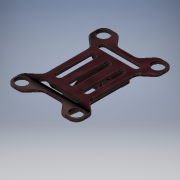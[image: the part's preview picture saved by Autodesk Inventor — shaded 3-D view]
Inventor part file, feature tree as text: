
AUTODESK INVENTOR PART (.ipt)
format: ipt  version: 2018 (Build 220112000, 112)  size: 1,005,056 bytes
history: native  units: in
note: dims shown in document units (in); Inventor stores cm internally (conversion verified against a paired STEP export)
features: fillet x13, extrude x9, sketch x9, delete_face x4, projected_geometry x2
ambient origin geometry x8: Origin, YZ Plane, XZ Plane, XY Plane, X Axis, Y Axis, Z Axis, Center Point
bodies: Solid1 (feature_tree)
feature tree (37):
  extrude  "Extrusion1"  Depth=0.189in
  extrude  "Extrusion2"  Depth=0.189in
  extrude  "Extrusion3"  Depth=0.0591in
  extrude  "Extrusion4"  Depth=1.1181in
  extrude  "Extrusion5"  Depth=0.5906in TaperAngle=0.0deg
  extrude  "Extrusion6"  Depth=0.315in
  delete_face  "Delete Face1"
  delete_face  "Delete Face2"
  delete_face  "Delete Face3"
  extrude  "Extrusion11"  Depth=0.1575in
  delete_face  "Delete Face4"
  extrude  "Extrusion12"  Depth=0.3937in TaperAngle=0.0deg
  extrude  "Extrusion13"  Depth=0.1181in TaperAngle=0.0deg
  fillet  "Fillet9"  Radius=0.0787in
  fillet  "Fillet11"  Radius=1.378in
  fillet  "Fillet15"  Radius=1.378in
  fillet  "Fillet22"  Radius=0.6299in
  fillet  "Fillet23"  Radius=0.0787in
  fillet  "Fillet24"  Radius=1.9291in
  fillet  "Fillet25"  Radius=2.6772in
  fillet  "Fillet26"  Radius=0.9646in
  fillet  "Fillet27"  Radius=1.3386in
  fillet  "Fillet28"  Radius=0.2953in
  fillet  "Fillet29"  Radius=0.748in
  fillet  "Fillet30"  Radius=1.122in
  fillet  "Fillet31"  Radius=0.8933in
  sketch  "Sketch1"  dims[d1=0.8976in d2=0.189in]
  sketch  "Sketch3"  dims[d3=0.0787in d6=0.189in]
  sketch  "Sketch4"  dims[d7=1.2756in d8=0.0591in]
  sketch  "Sketch5"  dims[d9=0.0591in d10=1.1181in]
  projected_geometry  "Projected Loop1"
  sketch  "Sketch6"  dims[d11=0.0394in d12=0.5906in d13=0.0in]
  sketch  "Sketch7"  dims[d15=3.937in d16=0.0in d17=0.315in]
  sketch  "Sketch12"  dims[d18=0.315in d19=0.1575in]
  sketch  "Sketch13"  dims[d20=0.3937in d21=0.0in d23=0.3307in d24=0.0in]
  projected_geometry  "Projected Loop5"
  sketch  "Sketch14"  dims[d29=0.7874in d30=0.0in d34=3.937in d35=0.0in d60=0.0787in d61=0.0in d68=1.378in d69=1.378in d70=0.6299in d71=0.0787in d72=0.0in d73=1.9291in d74=2.6772in d75=0.9646in d76=1.3386in d77=0.2953in d78=0.748in d79=1.122in d81=0.8933in d83=0.42in d85=0.1969in d86=0.315in d87=0.1575in d88=0.9213in d89=0.4606in d90=0.9213in d91=0.9213in d92=0.0787in d93=0.0in d94=0.0197in d96=0.0197in d100=0.0197in d107=0.0197in d108=0.0197in d109=0.0197in d110=0.0197in d111=0.0197in d112=0.0197in d113=0.0197in d114=0.0197in d115=0.0197in d116=0.1181in]
